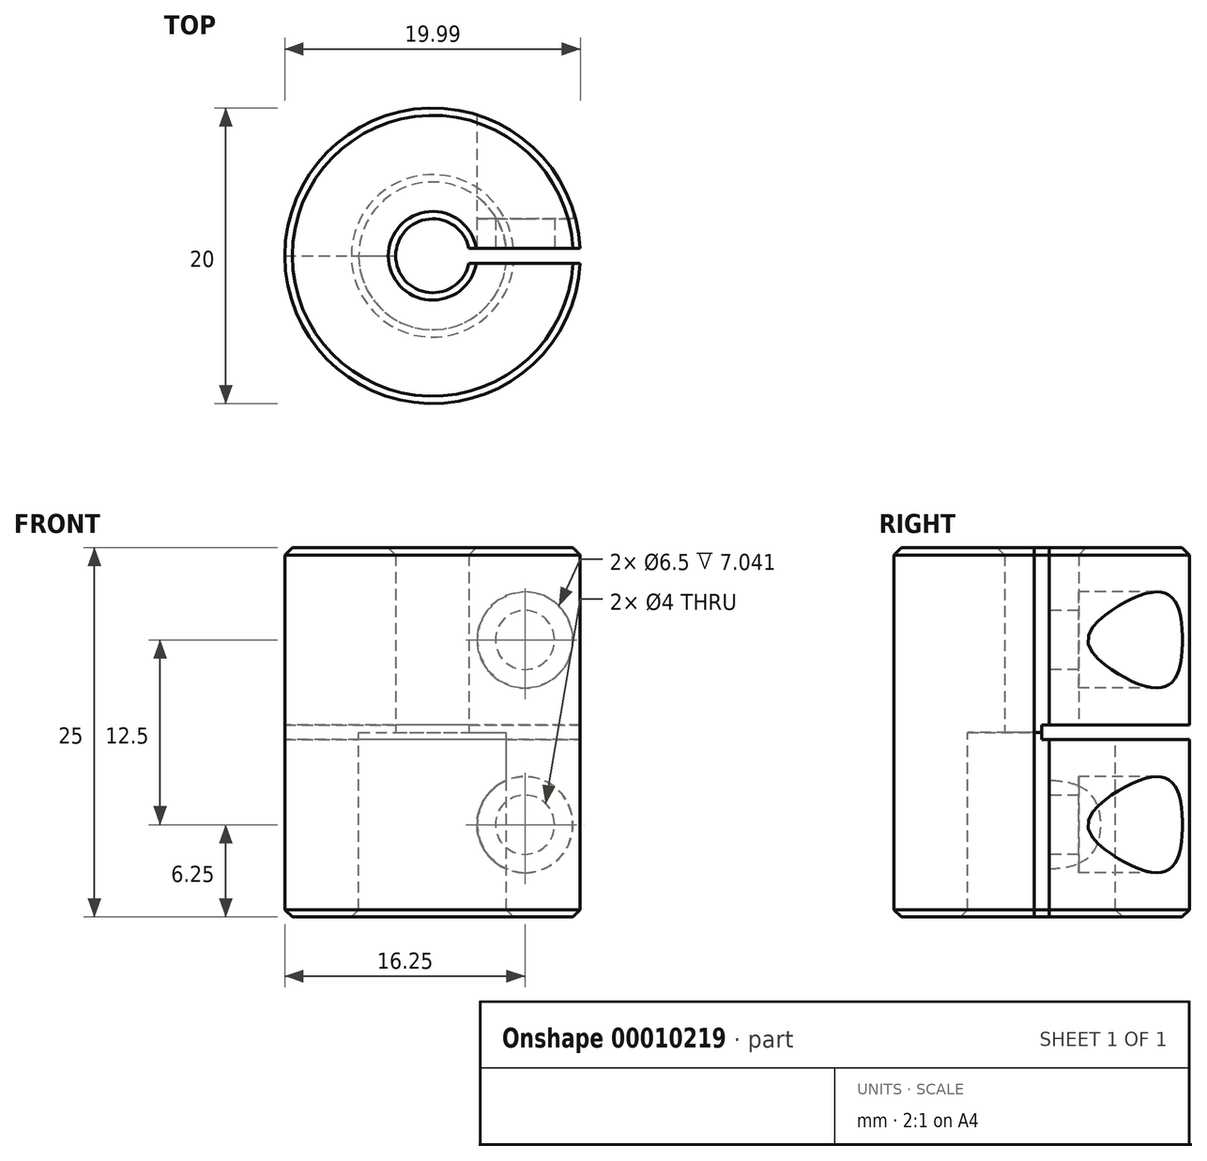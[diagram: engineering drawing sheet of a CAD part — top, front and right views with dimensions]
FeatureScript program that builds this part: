
annotation { "Feature Type Name" : "Feature", "Feature Type Description" : "" }
export const myFeature = defineFeature(function(context is Context, id is Id, definition is map)
    precondition{}
    {
        {
            assignVariable(context, id + "F0", {"name" : "ShaftDiameter1", "anyValue" : 5});
        }
        {
            assignVariable(context, id + "F1", {"name" : "CouplerHeight", "anyValue" : 25});
        }
        {
            assignVariable(context, id + "F2", {"name" : "CutWidth", "anyValue" : 1});
        }
        {
            var Q0;
            Q0=qCreatedBy(makeId("Top.planeOp"),FACE);
            var sketch = newSketch(context, id + "F3", { "sketchPlane" : qUnion([Q0])});
            skCircle(sketch, "E0", {"center": v(0, 0) * mm, "radius": 2.5 * mm});
            skCircle(sketch, "E1", {"center": v(0, 0) * mm, "radius": 5 * mm});
            skCircle(sketch, "E2", {"center": v(0, 0) * mm, "radius": 10 * mm});
            skLineSegment(sketch, "E3", {"start": v(-10, 0) * mm, "end": v(10, 0) * mm});
            skLineSegment(sketch, "E4", {"start": v(4.97, 0.5) * mm, "end": v(9.99, 0.5) * mm});
            skLineSegment(sketch, "E5.MirrorCS", {"start": v(4.97, -0.5) * mm, "end": v(9.99, -0.5) * mm});
            skLineSegment(sketch, "E6", {"start": v(4.97, 0.5) * mm, "end": v(2.45, 0.5) * mm});
            skLineSegment(sketch, "E7.MirrorCS", {"start": v(4.97, -0.5) * mm, "end": v(2.45, -0.5) * mm});
            skSolve(sketch);
        }
        {
            var Q0;
            {var subQ0=sQuery(id+"F3.wireOp",EDGE,"E5.MirrorCS");Q0=makeQuery(id+"F3.imprint","IMPRINT",FACE,{"disambiguationData":[TD([[makeQuery(id+"F3.imprint","IMPRINT",EDGE,{"derivedFrom":subQ0}),-1.0]])]});}
            var Q1;
            {var subQ0=sQuery(id+"F3.wireOp",EDGE,"E7.MirrorCS");Q1=makeQuery(id+"F3.imprint","IMPRINT",FACE,{"disambiguationData":[TD([[makeQuery(id+"F3.imprint","IMPRINT",EDGE,{"derivedFrom":subQ0}),1.0]])]});}
            extrude(context, id + "F4", {"entities" : qUnion([Q0, Q1]), "depth" : (getVariable(context, 'CutWidth') / 2) * mm, "offsetDistance" : 25 * mm});
        }
        {
            var Q0;
            {var subQ0=sQuery(id+"F3.wireOp",EDGE,"E5.MirrorCS");Q0=makeQuery(id+"F3.imprint","IMPRINT",FACE,{"disambiguationData":[TD([[makeQuery(id+"F3.imprint","IMPRINT",EDGE,{"derivedFrom":subQ0}),-1.0]])]});}
            extrude(context, id + "F5", {"entities" : qUnion([Q0]), "operationType" : NewBodyOperationType.ADD, "oppositeDirection" : true, "depth" : (getVariable(context, 'CutWidth') / 2) * mm, "offsetDistance" : 25 * mm});
        }
        {
            var Q0;
            {var subQ0=sQuery(id+"F3.wireOp",EDGE,"E5.MirrorCS");Q0=makeQuery(id+"F3.imprint","IMPRINT",FACE,{"disambiguationData":[TD([[makeQuery(id+"F3.imprint","IMPRINT",EDGE,{"derivedFrom":subQ0}),-1.0]])]});}
            var Q1;
            {var subQ0=sQuery(id+"F3.wireOp",EDGE,"E7.MirrorCS");Q1=makeQuery(id+"F3.imprint","IMPRINT",FACE,{"disambiguationData":[TD([[makeQuery(id+"F3.imprint","IMPRINT",EDGE,{"derivedFrom":subQ0}),1.0]])]});}
            var Q2;
            {var subQ0=sQuery(id+"F3.wireOp",EDGE,"E4");Q2=makeQuery(id+"F3.imprint","IMPRINT",FACE,{"disambiguationData":[TD([[makeQuery(id+"F3.imprint","IMPRINT",EDGE,{"derivedFrom":subQ0}),1.0]])]});}
            var Q3;
            {var subQ0=sQuery(id+"F3.wireOp",EDGE,"E6");Q3=makeQuery(id+"F3.imprint","IMPRINT",FACE,{"disambiguationData":[TD([[makeQuery(id+"F3.imprint","IMPRINT",EDGE,{"derivedFrom":subQ0}),-1.0]])]});}
            extrude(context, id + "F6", {"entities" : qUnion([Q0, Q1, Q2, Q3]), "operationType" : NewBodyOperationType.ADD, "depth" : (getVariable(context, 'CouplerHeight') / 2) * mm, "offsetDistance" : 25 * mm, "hasSecondDirection" : true, "secondDirectionOppositeDirection" : true, "secondDirectionDepth" : (-(getVariable(context, 'CutWidth') / 2)) * mm});
        }
        {
            var Q0;
            {var subQ0=sQuery(id+"F3.wireOp",EDGE,"E5.MirrorCS");Q0=makeQuery(id+"F3.imprint","IMPRINT",FACE,{"disambiguationData":[TD([[makeQuery(id+"F3.imprint","IMPRINT",EDGE,{"derivedFrom":subQ0}),-1.0]])]});}
            var Q1;
            {var subQ0=sQuery(id+"F3.wireOp",EDGE,"E4");Q1=makeQuery(id+"F3.imprint","IMPRINT",FACE,{"disambiguationData":[TD([[makeQuery(id+"F3.imprint","IMPRINT",EDGE,{"derivedFrom":subQ0}),1.0]])]});}
            extrude(context, id + "F7", {"entities" : qUnion([Q0, Q1]), "operationType" : NewBodyOperationType.ADD, "oppositeDirection" : true, "depth" : (getVariable(context, 'CouplerHeight') / 2) * mm, "offsetDistance" : 25 * mm, "hasSecondDirection" : true, "secondDirectionOppositeDirection" : false, "secondDirectionDepth" : (-(getVariable(context, 'CutWidth') / 2)) * mm});
        }
        {
            var Q0;
            Q0=makeQuery(id+"F6.opExtrude","CAP_EDGE",EDGE,{"disambiguationData":[OSD([sQuery(id+"F3.wireOp",EDGE,"E2")])],"isStart":false});
            var Q1;
            Q1=makeQuery(id+"F7.opExtrude","CAP_EDGE",EDGE,{"disambiguationData":[OSD([sQuery(id+"F3.wireOp",EDGE,"E2")])],"isStart":false});
            var Q2;
            Q2=makeQuery(id+"F6.opExtrude","CAP_EDGE",EDGE,{"disambiguationData":[OSD([sQuery(id+"F3.wireOp",EDGE,"E0")])],"isStart":false});
            var Q3;
            Q3=makeQuery(id+"F7.opExtrude","CAP_EDGE",EDGE,{"disambiguationData":[OSD([sQuery(id+"F3.wireOp",EDGE,"E1")])],"isStart":false});
            chamfer(context, id + "F8", {"entities" : qUnion([Q0, Q1, Q2, Q3]), "width" : 0.5 * mm, "tangentPropagation" : true});
        }
        {
            var Q0;
            Q0=qCreatedBy(makeId("Front.planeOp"),FACE);
            var sketch = newSketch(context, id + "F9", { "sketchPlane" : qUnion([Q0])});
            skLineSegment(sketch, "E8", {"start": v(0, 15.37) * mm, "end": v(0, -15.04) * mm, "construction": true});
            skLineSegment(sketch, "E9", {"start": v(15.7, 0) * mm, "end": v(-17.22, 0) * mm, "construction": true});
            skLineSegment(sketch, "E10.0", {"start": v(9.49, 12.5) * mm, "end": v(-9.5, 12.5) * mm, "construction": true});
            skLineSegment(sketch, "E11.0", {"start": v(9.99, 0.5) * mm, "end": v(-10, 0.5) * mm, "construction": true});
            skLineSegment(sketch, "E12.0", {"start": v(9.99, -0.5) * mm, "end": v(-10, -0.5) * mm, "construction": true});
            skLineSegment(sketch, "E13.0", {"start": v(9.49, -12.5) * mm, "end": v(-9.5, -12.5) * mm, "construction": true});
            skLineSegment(sketch, "E14.0", {"start": v(9.99, 12) * mm, "end": v(9.99, 0.5) * mm, "construction": true});
            skLineSegment(sketch, "E15", {"start": v(-10, -12) * mm, "end": v(-10, 12) * mm, "construction": true});
            skLineSegment(sketch, "E16.0", {"start": v(9.99, -12) * mm, "end": v(9.99, -0.5) * mm, "construction": true});
            skCircle(sketch, "E17", {"center": v(6.25, 6.25) * mm, "radius": 2 * mm});
            skCircle(sketch, "E18", {"center": v(6.25, 6.25) * mm, "radius": 3.25 * mm});
            skCircle(sketch, "E19", {"center": v(6.25, -6.25) * mm, "radius": 2 * mm});
            skCircle(sketch, "E20", {"center": v(6.25, -6.25) * mm, "radius": 3.25 * mm});
            skSolve(sketch);
        }
        {
            var Q0;
            Q0=makeQuery(id+"F9.imprint","IMPRINT",FACE,{"disambiguationData":[TD([[makeQuery(id+"F9.imprint","IMPRINT",EDGE,{"derivedFrom":sQuery(id+"F9.wireOp",EDGE,"E17")}),-1.0]])]});
            var Q1;
            Q1=makeQuery(id+"F9.imprint","IMPRINT",FACE,{"disambiguationData":[TD([[makeQuery(id+"F9.imprint","IMPRINT",EDGE,{"derivedFrom":sQuery(id+"F9.wireOp",EDGE,"E17")}),1.0]])]});
            var Q2;
            Q2=makeQuery(id+"F9.imprint","IMPRINT",FACE,{"disambiguationData":[TD([[makeQuery(id+"F9.imprint","IMPRINT",EDGE,{"derivedFrom":sQuery(id+"F9.wireOp",EDGE,"E19")}),-1.0]])]});
            var Q3;
            Q3=makeQuery(id+"F9.imprint","IMPRINT",FACE,{"disambiguationData":[TD([[makeQuery(id+"F9.imprint","IMPRINT",EDGE,{"derivedFrom":sQuery(id+"F9.wireOp",EDGE,"E19")}),1.0]])]});
            extrude(context, id + "F10", {"entities" : qUnion([Q0, Q1, Q2, Q3]), "operationType" : NewBodyOperationType.REMOVE, "endBound" : BoundingType.THROUGH_ALL, "oppositeDirection" : true, "depth" : 25 * mm, "hasOffset" : true, "offsetDistance" : (getVariable(context, 'CutWidth') / 2) * mm});
        }
        {
            var Q0;
            Q0=makeQuery(id+"F9.imprint","IMPRINT",FACE,{"disambiguationData":[TD([[makeQuery(id+"F9.imprint","IMPRINT",EDGE,{"derivedFrom":sQuery(id+"F9.wireOp",EDGE,"E17")}),-1.0]])]});
            var Q1;
            Q1=makeQuery(id+"F9.imprint","IMPRINT",FACE,{"disambiguationData":[TD([[makeQuery(id+"F9.imprint","IMPRINT",EDGE,{"derivedFrom":sQuery(id+"F9.wireOp",EDGE,"E19")}),-1.0]])]});
            extrude(context, id + "F11", {"entities" : qUnion([Q0, Q1]), "operationType" : NewBodyOperationType.ADD, "oppositeDirection" : true, "depth" : (getVariable(context, 'ShaftDiameter1') / 2) * mm, "offsetDistance" : 25 * mm, "hasSecondDirection" : true, "secondDirectionOppositeDirection" : false, "secondDirectionDepth" : (-(getVariable(context, 'CutWidth') / 2)) * mm});
        }
    });
